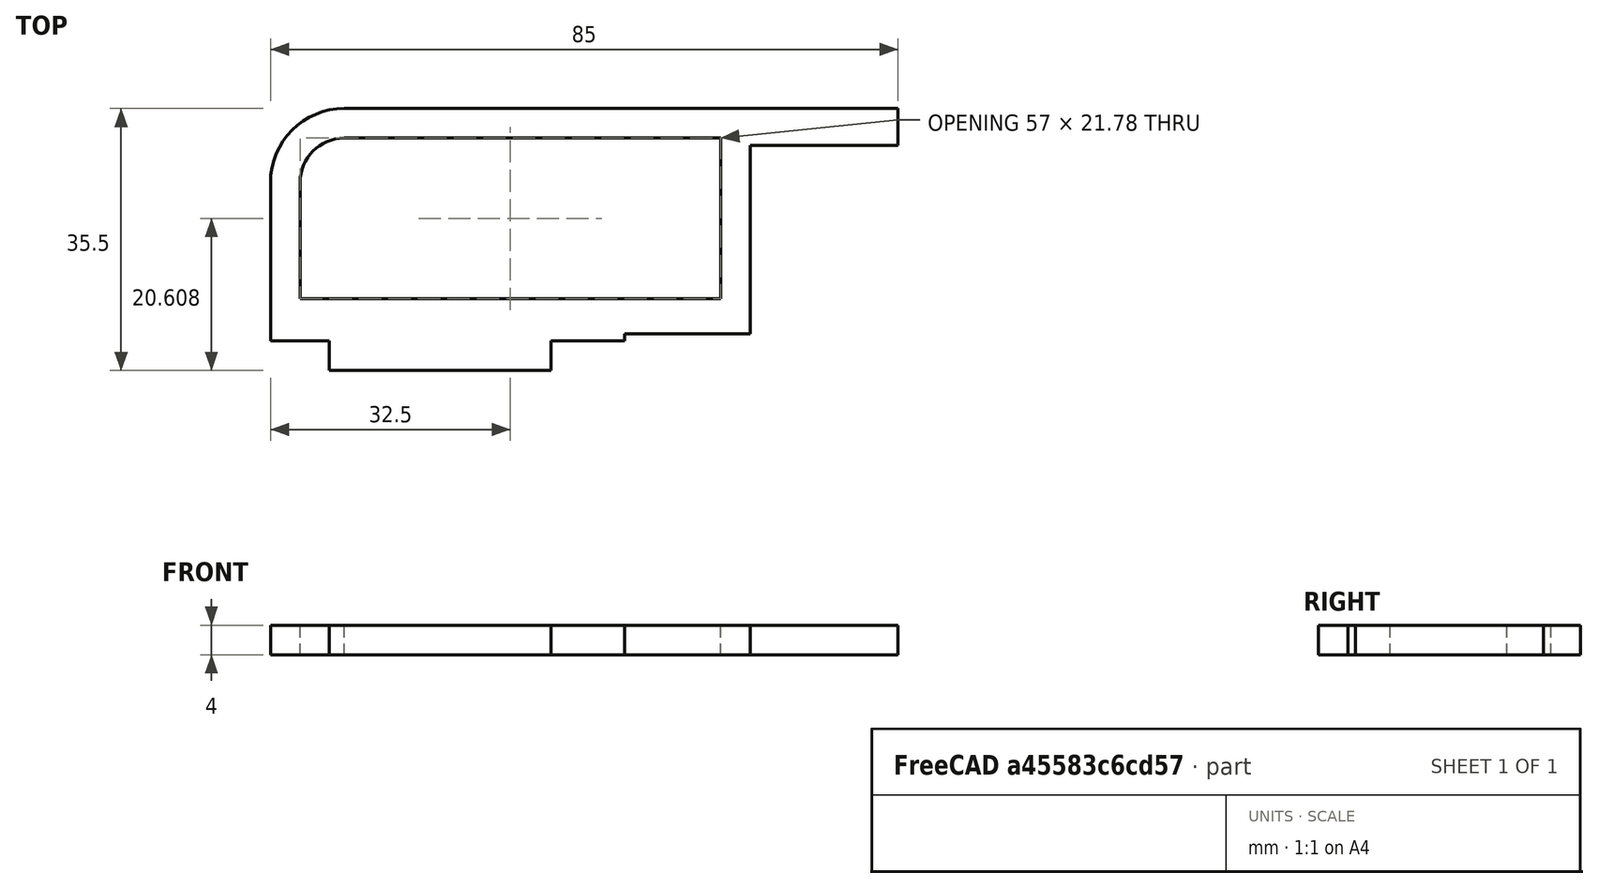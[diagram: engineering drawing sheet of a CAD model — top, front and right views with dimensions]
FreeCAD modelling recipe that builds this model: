
FCSTD DOCUMENT  (FreeCAD 0.21R33771 (Git))
Label: FRAME_STRUT_01
License: All rights reserved
LicenseURL: https://en.wikipedia.org/wiki/All_rights_reserved
objects: Sketcher::SketchObject×1, PartDesign::Pad×1, PartDesign::Body×1
note: 4 computed .brp shape members not serialized (recipe doc carries the construction recipe); baked Part::Feature solids carry a one-line shape summary decoded from their .brp

FEATURE [Sketcher::SketchObject] Sketch002  label="STRUT_01"
  FullyConstrained = false
  MapMode = 5
  sketch-geometry (30):
    g0: LineSegment StartX=65 StartY=31.5 StartZ=0 EndX=-10 EndY=31.5 EndZ=0
    g1: LineSegment StartX=-20 StartY=21.5 StartZ=0 EndX=-20 EndY=0 EndZ=0
    g2: LineSegment StartX=-20 StartY=0 StartZ=0 EndX=0 EndY=0 EndZ=0
    g3: LineSegment StartX=28 StartY=26.5 StartZ=0 EndX=65 EndY=26.5 EndZ=0
    g4: LineSegment StartX=65 StartY=26.5 StartZ=0 EndX=65 EndY=31.5 EndZ=0
    g5: LineSegment StartX=45 StartY=26.5 StartZ=0 EndX=65 EndY=26.5 EndZ=0
    g6: ArcOfCircle CenterX=-10 CenterY=21.5 CenterZ=0 NormalX=0 NormalY=0 NormalZ=1 AngleXU=0 Radius=10 StartAngle=1.5708 EndAngle=3.14159
    g7: GeomPoint X=-20 Y=31.5 Z=0
    g8: LineSegment StartX=28 StartY=0 StartZ=0 EndX=28 EndY=1 EndZ=0
    g9: LineSegment StartX=28 StartY=1 StartZ=0 EndX=45 EndY=1 EndZ=0
    g10: LineSegment StartX=45 StartY=1 StartZ=0 EndX=45 EndY=26.5 EndZ=0
    g11: LineSegment StartX=35 StartY=0 StartZ=0 EndX=45 EndY=0 EndZ=0
    g12: LineSegment StartX=45 StartY=0 StartZ=0 EndX=45 EndY=1 EndZ=0
    g13: LineSegment StartX=-10 StartY=31.5 StartZ=0 EndX=-10 EndY=27.5 EndZ=0
    g14: LineSegment StartX=-20 StartY=21.5 StartZ=0 EndX=-16 EndY=21.5 EndZ=0
    g15: LineSegment StartX=0 StartY=0 StartZ=0 EndX=0 EndY=5.71593 EndZ=0
    g16: LineSegment StartX=-16 StartY=21.5 StartZ=0 EndX=-16 EndY=5.71593 EndZ=0
    g17: LineSegment StartX=-16 StartY=5.71593 StartZ=0 EndX=0 EndY=5.71593 EndZ=0
    g18: LineSegment StartX=0 StartY=5.71593 StartZ=0 EndX=35 EndY=5.71593 EndZ=0
    g19: LineSegment StartX=35 StartY=5.71593 StartZ=0 EndX=41 EndY=5.71593 EndZ=0
    g20: LineSegment StartX=41 StartY=5.71593 StartZ=0 EndX=45 EndY=5.71593 EndZ=0
    g21: LineSegment StartX=41 StartY=5.71593 StartZ=0 EndX=41 EndY=27.5 EndZ=0
    g22: LineSegment StartX=41 StartY=27.5 StartZ=0 EndX=-10 EndY=27.5 EndZ=0
    g23: ArcOfCircle CenterX=-9.93259 CenterY=21.4326 CenterZ=0 NormalX=0 NormalY=0 NormalZ=1 AngleXU=0 Radius=6.06779 StartAngle=1.58191 EndAngle=3.13048
    g24: LineSegment StartX=28 StartY=0 StartZ=0 EndX=18 EndY=0 EndZ=0
    g25: LineSegment StartX=18 StartY=-4 StartZ=0 EndX=18 EndY=0 EndZ=0
    g26: LineSegment StartX=28 StartY=26.5 StartZ=0 EndX=28 EndY=1 EndZ=0
    g27: LineSegment StartX=18 StartY=-4 StartZ=0 EndX=-12 EndY=-4 EndZ=0
    g28: LineSegment StartX=-12 StartY=-4 StartZ=0 EndX=-12 EndY=0 EndZ=0
    g29: LineSegment StartX=-12 StartY=0 StartZ=0 EndX=-20 EndY=0 EndZ=0
  constraints (78):
    c: Horizontal(g0)
    c: Vertical(g1)
    c: Coincident(g2,g1)
    c: Horizontal(g3)
    c: Coincident(g4,g3)
    c: Coincident(g4,g0)
    c: Vertical(g4)
    c: Horizontal(g2)
    c: DistanceX(g7,g0) = 85
    c: DistanceX(g2,g2) = 20
    c: DistanceY(g4,g4) = 5
    c: PointOnObject(g5,g3)
    c: Coincident(g5,g3)
    c: DistanceY(g25,g8) = 4
    c: PointOnObject(g7,g0)
    c: PointOnObject(g7,g1)
    c: Tangent(g0,g6) = -1.5708
    c: Tangent(g1,g6) = -1.5708
    c: Radius(g6) = 10
    c: Coincident(g2,g-1)
    c: DistanceX(g5,g5) = 20
    c: Coincident(g9,g8)
    c: Horizontal(g9)
    c: Coincident(g10,g9)
    c: Coincident(g10,g5)
    c: Vertical(g10)
    c: DistanceY(g8,g5) = 26.5
    c: DistanceY(g8,g8) = 1
    c: PointOnObject(g8,g-1)
    c: PointOnObject(g11,g-1)
    c: Coincident(g12,g11)
    c: Coincident(g12,g9)
    c: Vertical(g12)
    c: Coincident(g13,g0)
    c: Vertical(g13)
    c: Coincident(g14,g1)
    c: Horizontal(g14)
    c: Coincident(g15,g2)
    c: PointOnObject(g15,g-2)
    c: Coincident(g16,g14)
    c: Vertical(g16)
    c: Coincident(g17,g16)
    c: Coincident(g17,g15)
    c: Horizontal(g17)
    c: Coincident(g18,g15)
    c: Horizontal(g19)
    c: Coincident(g20,g19)
    c: PointOnObject(g20,g10)
    c: Horizontal(g20)
    c: Horizontal(g18)
    c: DistanceX(g20,g20) = 4
    c: Equal(g20,g14)
    c: Equal(g14,g13)
    c: Coincident(g21,g19)
    c: Coincident(g22,g21)
    c: Coincident(g22,g13)
    c: Horizontal(g22)
    c: Vertical(g21)
    c: Coincident(g23,g14)
    c: Coincident(g23,g13)
    c: Coincident(g24,g8)
    c: PointOnObject(g24,g-1)
    c: Coincident(g25,g24)
    c: Vertical(g25)
    c: DistanceX(g9,g9) = 17
    c: Vertical(g8)
    c: Vertical(g3,g8)
    c: Coincident(g26,g3)
    c: Coincident(g26,g8)
    c: Coincident(g27,g25)
    c: Horizontal(g27)
    c: Coincident(g28,g27)
    c: PointOnObject(g28,g2)
    c: Vertical(g28)
    c: Coincident(g29,g28)
    c: Coincident(g29,g1)
    c: DistanceX(g27,g27) = 30
    c: DistanceX(g24,g24) = 10
FEATURE [PartDesign::Pad] Pad
  Direction = (0,0,1)
  Length = 4
  Length2 = 10
  Profile = -> Sketch002
  ReferenceAxis = -> Sketch002 [N_Axis]
  Refine = true
  Type = 0
FEATURE [PartDesign::Body] Body
  Group = -> [Sketch002,Pad]
  Origin = -> Origin
  Tip = -> Pad
